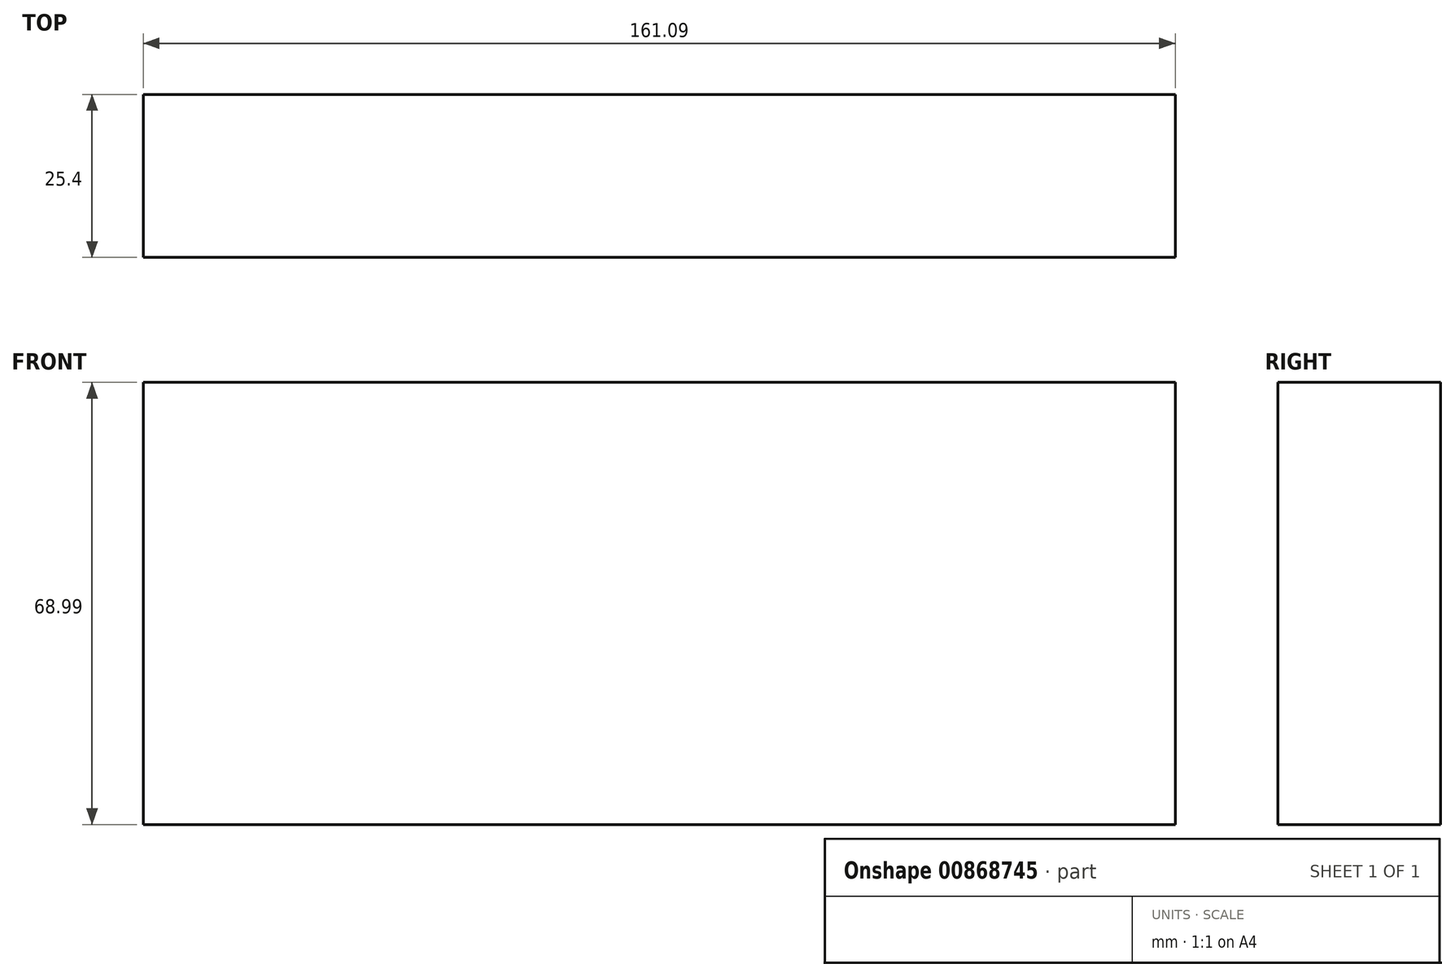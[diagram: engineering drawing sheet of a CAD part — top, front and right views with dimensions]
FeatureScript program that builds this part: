
annotation { "Feature Type Name" : "Feature", "Feature Type Description" : "" }
export const myFeature = defineFeature(function(context is Context, id is Id, definition is map)
    precondition{}
    {
        {
            var Q0;
            Q0=qCreatedBy(makeId("Front.planeOp"),FACE);
            var sketch = newSketch(context, id + "F0", { "sketchPlane" : qUnion([Q0])});
            skLineSegment(sketch, "E0.bottom", {"start": v(-97.01, 49.5) * mm, "end": v(64.08, 49.5) * mm});
            skLineSegment(sketch, "E0.top", {"start": v(-97.01, -19.5) * mm, "end": v(64.08, -19.5) * mm});
            skLineSegment(sketch, "E0.left", {"start": v(-97.01, 49.5) * mm, "end": v(-97.01, -19.5) * mm});
            skLineSegment(sketch, "E0.right", {"start": v(64.08, 49.5) * mm, "end": v(64.08, -19.5) * mm});
            skSolve(sketch);
        }
        {
            var Q0;
            Q0=makeQuery(id+"F0.imprint","IMPRINT",FACE,{"disambiguationData":[TD([[makeQuery(id+"F0.imprint","IMPRINT",EDGE,{"derivedFrom":sQuery(id+"F0.wireOp",EDGE,"E0.bottom")}),-1.0]])]});
            extrude(context, id + "F1", {"entities" : qUnion([Q0]), "depth" : 25.4 * mm, "offsetDistance" : 25.4 * mm});
        }
    });
